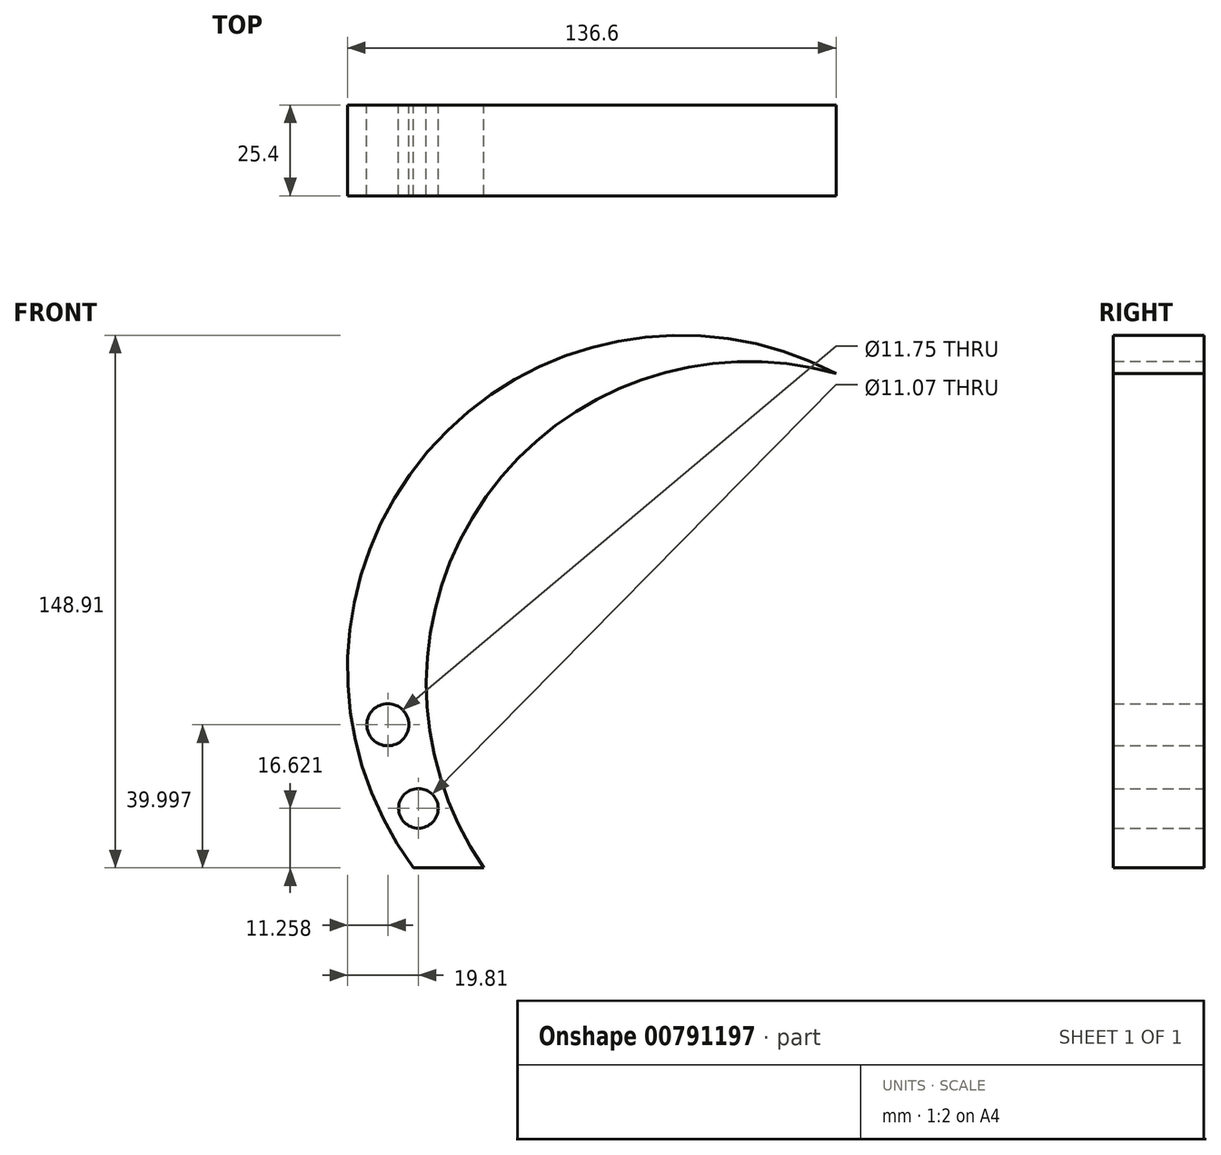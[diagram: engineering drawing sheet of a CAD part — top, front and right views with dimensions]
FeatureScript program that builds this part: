
annotation { "Feature Type Name" : "Feature", "Feature Type Description" : "" }
export const myFeature = defineFeature(function(context is Context, id is Id, definition is map)
    precondition{}
    {
        {
            var Q0;
            Q0=qCreatedBy(makeId("Front.planeOp"),FACE);
            var sketch = newSketch(context, id + "F0", { "sketchPlane" : qUnion([Q0])});
            skArc(sketch, "E0", {"start": v(53.16, 66.21) * mm, "mid": v(-61.06, 44.3) * mm, "end": v(-65.03, -71.92) * mm});
            skArc(sketch, "E1", {"start": v(53.16, 66.21) * mm, "mid": v(-44.7, 31.76) * mm, "end": v(-45.3, -71.99) * mm});
            skLineSegment(sketch, "E2", {"start": v(-65.03, -71.92) * mm, "end": v(-45.3, -71.99) * mm});
            skSolve(sketch);
        }
        {
            var Q0;
            Q0 = qSketchRegion(id + "F0", true);
            extrude(context, id + "F1", {"entities" : qUnion([Q0]), "depth" : 25.4 * mm, "offsetDistance" : 25.4 * mm});
        }
        {
            var Q0;
            Q0=qCreatedBy(makeId("Front.planeOp"),FACE);
            var sketch = newSketch(context, id + "F2", { "sketchPlane" : qUnion([Q0])});
            skCircle(sketch, "E3", {"center": v(-63.63, -55.37) * mm, "radius": 5.54 * mm});
            skCircle(sketch, "E4", {"center": v(-72.18, -32) * mm, "radius": 5.88 * mm});
            skSolve(sketch);
        }
        {
            var Q0;
            Q0 = qSketchRegion(id + "F2", true);
            extrude(context, id + "F3", {"entities" : qUnion([Q0]), "operationType" : NewBodyOperationType.REMOVE, "depth" : 73.4 * mm, "offsetDistance" : 25.4 * mm});
        }
    });
